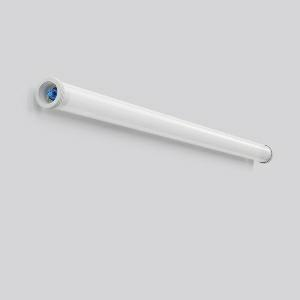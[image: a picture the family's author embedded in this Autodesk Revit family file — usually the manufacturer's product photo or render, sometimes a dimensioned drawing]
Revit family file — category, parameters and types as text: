
# Revit family: planox_tube_601072_002_730hf_7510
name_source: partatom
category: Lighting Fixtures
units: mm (PartAtom-declared; Revit-internal decimal feet)

## family parameters
Cut with Voids When Loaded = No
Host = Face
Light Source = No
Part Type = Normal
Room Calculation Point = No
Round Connector Dimension = Use Diameter
Shared = No

## types (1)
- PLANOX TUBE (1 x LED Modul 840, 8650 lm, 4000)
    Apparent Load = 62 VA
    CIE Flux Codes = 42 71 90 91 100
    Color Rendering = 80
    Color Temperature = 4000
    Default Elevation = 1800 mm
    Description = Series: PLANOX TUBE
Robust protective tube luminaire for tough requirements. Rack made of sheet steel, white powder coated. End caps made of plastic (polyamide) grey. Diffuser made of plastic (polycarbonate), opal, shockproof. Symmetrical light distribution. Homogeneous light distribution. With accessories for wall, ceiling or pendant mounting. Mounting set must be ordered separately. Luminaire with limited surface temperature in accordance with EN 60598-2-24 for use in environments in which a deposit of conductive dust on the luminaire can be expected. Qualified for use in the food and drink industry. Suitable for lighting in public car parks and public off-street parking spaces according to DIN 67528. Environmentally friendly and resource-saving due to replaceable components. 
Colour: white
Diameter: 78 mm
Length: 1631 mm
Lamp: LED
Socket: without socket
Colour temperature: 4000K
Colour rendering index (CRI): 83
System power: 62 W
Rated luminous flux: 8650 lm
Luminous efficiency: 140 lm/W
Control gear: Dimmable Bluetooth converter
Protection class: I
Type of protection: IP 67
    Height = 0 mm  [stored 0 ft]
    Lamp = 1 x LED Modul 840
    Lamp Light Flux = 8650 lm
    Lamp count = 1
    Length = 1631 mm
    Lifetime = 50000 h
    Luminous efficacy = 140 lm/W
    Manufacturer = RZB
    ModVariant = No
    Model = 601072.002.730HF
    Mounting Place = Wall, Ceiling
    Mounting Type = Surface mounted
    Number of Poles = 1
    OnlyDefault = Yes
    Power Factor = 1
    Product Name = PLANOX TUBE
    Product group = Surface mounted luminaires for moist/humid enviroments
    ProductGroupID = 308
    Protection Class = Protection class I
    Protection Degree = Degree of protection
    RLX_Detail_Level = 1
    RLX_Emergency_Light_Flux = 0 lm
    RLX_Emergency_Type = 0
    RLX_Emergency_Type_DB = No
    RlxData = <blob elided: 34769 chars, md5=7ca8ec53>
    Socket = socket
    Standby Power = 0 W
    System Light Flux = 8650 lm
    System Power = 62 W
    Type Comments = Product without accessories
    Type Image = 601072.002.jpg
    URL = http://relux.com
    VarID = ---
    Voltage = 230 V
    Voltage Range = 220-240 V
    Weight = 0.00 kg
    Width = 0 mm  [stored 0 ft]

note: [stored X ft] marks values corroborated as IEEE doubles in the binary element streams (Revit-internal decimal feet)

## geometry (parser evidence)
native form markers: Blend x4, Sweep x13
no freeform markers — native parametric forms only
